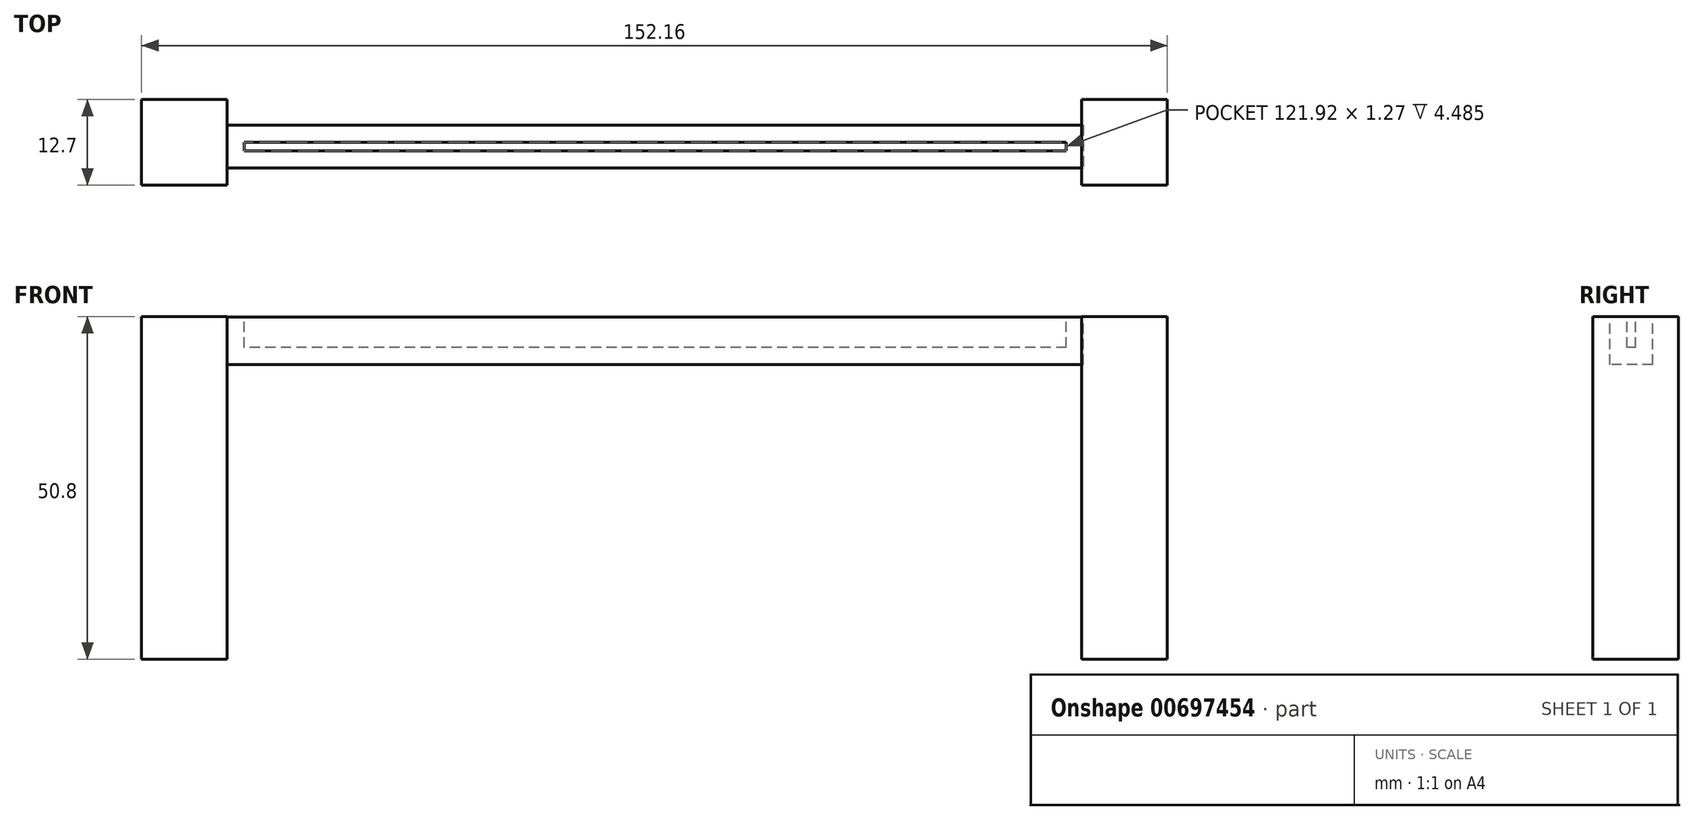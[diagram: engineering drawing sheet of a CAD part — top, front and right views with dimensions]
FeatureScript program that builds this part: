
annotation { "Feature Type Name" : "Feature", "Feature Type Description" : "" }
export const myFeature = defineFeature(function(context is Context, id is Id, definition is map)
    precondition{}
    {
        {
            var Q0;
            Q0=qCreatedBy(makeId("Top.planeOp"),FACE);
            var sketch = newSketch(context, id + "F0", { "sketchPlane" : qUnion([Q0])});
            skLineSegment(sketch, "E0.bottom", {"start": v(-76.08, 6.6) * mm, "end": v(-63.38, 6.6) * mm});
            skLineSegment(sketch, "E0.top", {"start": v(-76.08, -6.1) * mm, "end": v(-63.38, -6.1) * mm});
            skLineSegment(sketch, "E0.left", {"start": v(-76.08, 6.6) * mm, "end": v(-76.08, -6.1) * mm});
            skLineSegment(sketch, "E0.right", {"start": v(-63.38, 6.6) * mm, "end": v(-63.38, -6.1) * mm});
            skLineSegment(sketch, "E1.MirrorCS", {"start": v(76.08, 6.6) * mm, "end": v(63.38, 6.6) * mm});
            skLineSegment(sketch, "E2.MirrorCS", {"start": v(63.38, 6.6) * mm, "end": v(63.38, -6.1) * mm});
            skLineSegment(sketch, "E3.MirrorCS", {"start": v(76.08, 6.6) * mm, "end": v(76.08, -6.1) * mm});
            skLineSegment(sketch, "E4.MirrorCS", {"start": v(76.08, -6.1) * mm, "end": v(63.38, -6.1) * mm});
            skSolve(sketch);
        }
        {
            var Q0;
            Q0=makeQuery(id+"F0.imprint","IMPRINT",FACE,{"disambiguationData":[TD([[makeQuery(id+"F0.imprint","IMPRINT",EDGE,{"derivedFrom":sQuery(id+"F0.wireOp",EDGE,"E0.bottom")}),-1.0]])]});
            var Q1;
            Q1=makeQuery(id+"F0.imprint","IMPRINT",FACE,{"disambiguationData":[TD([[makeQuery(id+"F0.imprint","IMPRINT",EDGE,{"derivedFrom":sQuery(id+"F0.wireOp",EDGE,"E1.MirrorCS")}),1.0]])]});
            extrude(context, id + "F1", {"entities" : qUnion([Q0, Q1]), "depth" : 50.8 * mm, "offsetDistance" : 25.4 * mm});
        }
        {
            var Q0;
            Q0=makeQuery(id+"F1.opExtrude","SWEPT_FACE",FACE,{"disambiguationData":[OSD([sQuery(id+"F0.wireOp",EDGE,"E0.right")])]});
            var sketch = newSketch(context, id + "F2", { "sketchPlane" : qUnion([Q0])});
            skPoint(sketch, "E5.firstSnap0", {"position": v(2.8, 50.71) * mm});
            skLineSegment(sketch, "E5.bottom", {"start": v(2.8, 43.69) * mm, "end": v(-3.56, 43.69) * mm});
            skLineSegment(sketch, "E5.top", {"start": v(2.8, 50.71) * mm, "end": v(-3.56, 50.71) * mm});
            skLineSegment(sketch, "E5.left", {"start": v(2.8, 43.69) * mm, "end": v(2.8, 50.71) * mm});
            skLineSegment(sketch, "E5.right", {"start": v(-3.56, 43.69) * mm, "end": v(-3.56, 50.71) * mm});
            skSolve(sketch);
        }
        {
            var Q0;
            Q0 = qSketchRegion(id + "F2", true);
            extrude(context, id + "F3", {"entities" : qUnion([Q0]), "depth" : 127 * mm, "offsetDistance" : 25.4 * mm});
        }
        {
            var Q0;
            Q0=makeQuery(id+"F3.opExtrude","SWEPT_FACE",FACE,{"disambiguationData":[OSD([sQuery(id+"F2.wireOp",EDGE,"E5.top")])]});
            shell(context, id + "F4", {"entities" : qUnion([Q0]), "thickness" : 2.54 * mm});
        }
    });
